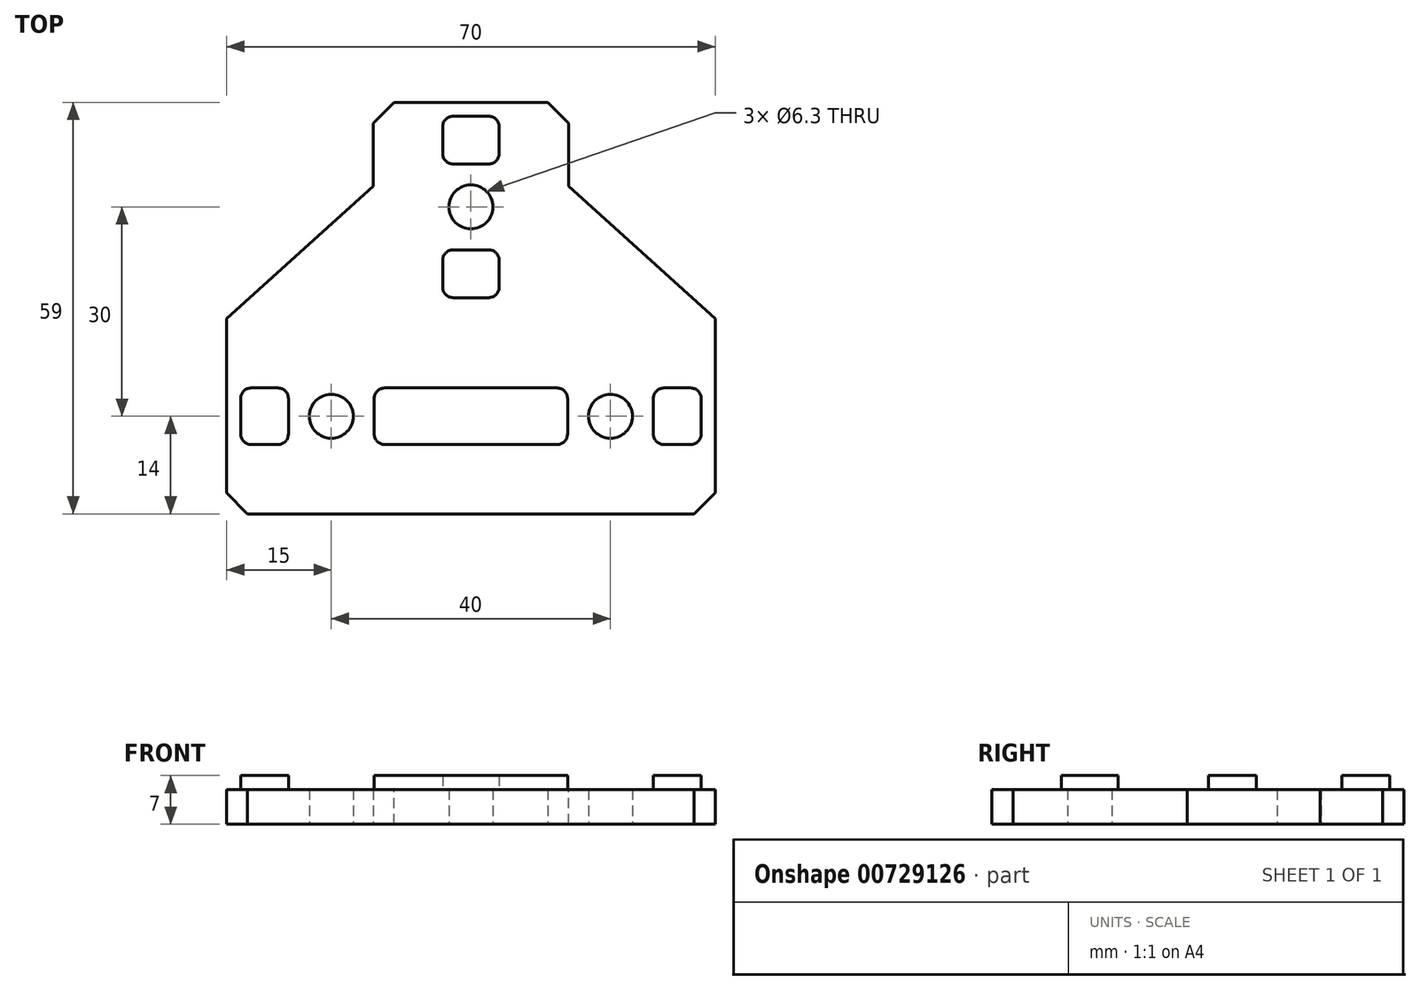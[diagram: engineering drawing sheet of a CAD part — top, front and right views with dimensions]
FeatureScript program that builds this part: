
annotation { "Feature Type Name" : "Feature", "Feature Type Description" : "" }
export const myFeature = defineFeature(function(context is Context, id is Id, definition is map)
    precondition{}
    {
        {
            var Q0;
            Q0=qCreatedBy(makeId("Top.planeOp"),FACE);
            var sketch = newSketch(context, id + "F0", { "sketchPlane" : qUnion([Q0])});
            skLineSegment(sketch, "E0", {"start": v(-35, 0) * mm, "end": v(-35, 28) * mm});
            skLineSegment(sketch, "E1", {"start": v(-35, 28) * mm, "end": v(-14, 47) * mm});
            skLineSegment(sketch, "E2", {"start": v(14, 47) * mm, "end": v(35, 28) * mm});
            skLineSegment(sketch, "E3", {"start": v(35, 28) * mm, "end": v(35, 0) * mm});
            skLineSegment(sketch, "E4", {"start": v(35, 0) * mm, "end": v(-35, 0) * mm});
            skPoint(sketch, "E5", {"position": v(0, 0) * mm});
            skLineSegment(sketch, "E6", {"start": v(-14, 47) * mm, "end": v(-14, 59) * mm});
            skLineSegment(sketch, "E7", {"start": v(-14, 59) * mm, "end": v(14, 59) * mm});
            skLineSegment(sketch, "E8", {"start": v(14, 59) * mm, "end": v(14, 47) * mm});
            skPoint(sketch, "E9", {"position": v(0, 59) * mm});
            skPoint(sketch, "E10.centerSnap0", {"position": v(-35, 14) * mm});
            skPoint(sketch, "E11.centerSnap0", {"position": v(35, 14) * mm});
            skPoint(sketch, "E12", {"position": v(0, 44) * mm});
            skPoint(sketch, "E13", {"position": v(-20, 14) * mm});
            skPoint(sketch, "E14", {"position": v(20, 14) * mm});
            skSolve(sketch);
        }
        {
            var Q0;
            Q0=makeQuery(id+"F0.imprint","IMPRINT",FACE,{"disambiguationData":[TD([[makeQuery(id+"F0.imprint","IMPRINT",EDGE,{"derivedFrom":sQuery(id+"F0.wireOp",EDGE,"E0")}),-1.0]])]});
            extrude(context, id + "F1", {"entities" : qUnion([Q0]), "oppositeDirection" : true, "depth" : 5 * mm, "offsetDistance" : 25 * mm});
        }
        {
            var Q0;
            Q0=sQuery(id+"F0.wireOp",VERTEX,"E14");
            var Q1;
            Q1=sQuery(id+"F0.wireOp",VERTEX,"E13");
            var Q2;
            Q2=sQuery(id+"F0.wireOp",VERTEX,"E12");
            var Q3;
            Q3=makeQuery(id+"F1.opExtrude","SWEPT_BODY",BODY,{"disambiguationData":[OSD([sQuery(id+"F0.wireOp",EDGE,"E0"),sQuery(id+"F0.wireOp",EDGE,"E1"),sQuery(id+"F0.wireOp",EDGE,"E2"),sQuery(id+"F0.wireOp",EDGE,"E3"),sQuery(id+"F0.wireOp",EDGE,"E4"),sQuery(id+"F0.wireOp",EDGE,"E6"),sQuery(id+"F0.wireOp",EDGE,"E7"),sQuery(id+"F0.wireOp",EDGE,"E8")])]});
            hole(context, id + "F2", {"style" : HoleStyle.SIMPLE, "endStyle" : HoleEndStyle.THROUGH, "holeDiameter" : 6.3 * mm, "majorDiameter" : 5 * mm, "isTappedThrough" : true, "tappedDepth" : 12 * mm, "tapClearance" : 3, "locations" : qUnion([Q0, Q1, Q2]), "scope" : qUnion([Q3]), "startStyle" : HoleStartStyle.PART});
        }
        {
            var Q0;
            Q0=makeQuery(id+"F1.opExtrude","SWEPT_EDGE",EDGE,{"disambiguationData":[OSD([sQuery(id+"F0.wireOp",EDGE,"E7"),sQuery(id+"F0.wireOp",EDGE,"E8")])]});
            var Q1;
            Q1=makeQuery(id+"F1.opExtrude","SWEPT_EDGE",EDGE,{"disambiguationData":[OSD([sQuery(id+"F0.wireOp",EDGE,"E6"),sQuery(id+"F0.wireOp",EDGE,"E7")])]});
            var Q2;
            Q2=makeQuery(id+"F1.opExtrude","SWEPT_EDGE",EDGE,{"disambiguationData":[OSD([sQuery(id+"F0.wireOp",EDGE,"E3"),sQuery(id+"F0.wireOp",EDGE,"E4")])]});
            var Q3;
            Q3=makeQuery(id+"F1.opExtrude","SWEPT_EDGE",EDGE,{"disambiguationData":[OSD([sQuery(id+"F0.wireOp",EDGE,"E0"),sQuery(id+"F0.wireOp",EDGE,"E4")])]});
            chamfer(context, id + "F3", {"entities" : qUnion([Q0, Q1, Q2, Q3]), "width" : 3 * mm, "tangentPropagation" : true});
        }
        {
            var Q0;
            Q0=makeQuery(id+"F1.opExtrude","CAP_FACE",FACE,{"disambiguationData":[OSD([sQuery(id+"F0.wireOp",EDGE,"E0"),sQuery(id+"F0.wireOp",EDGE,"E1"),sQuery(id+"F0.wireOp",EDGE,"E2"),sQuery(id+"F0.wireOp",EDGE,"E3"),sQuery(id+"F0.wireOp",EDGE,"E4"),sQuery(id+"F0.wireOp",EDGE,"E6"),sQuery(id+"F0.wireOp",EDGE,"E7"),sQuery(id+"F0.wireOp",EDGE,"E8")])],"isStart":true});
            var sketch = newSketch(context, id + "F4", { "sketchPlane" : qUnion([Q0])});
            skLineSegment(sketch, "E15.bottom", {"start": v(-26.15, 18.05) * mm, "end": v(-33, 18.05) * mm});
            skLineSegment(sketch, "E15.top", {"start": v(-26.15, 9.95) * mm, "end": v(-33, 9.95) * mm});
            skLineSegment(sketch, "E15.left", {"start": v(-26.15, 18.05) * mm, "end": v(-26.15, 9.95) * mm});
            skLineSegment(sketch, "E15.right", {"start": v(-33, 18.05) * mm, "end": v(-33, 9.95) * mm});
            skLineSegment(sketch, "E16.bottom", {"start": v(-13.85, 18.05) * mm, "end": v(13.85, 18.05) * mm});
            skLineSegment(sketch, "E16.top", {"start": v(-13.85, 9.95) * mm, "end": v(13.85, 9.95) * mm});
            skLineSegment(sketch, "E16.left", {"start": v(-13.85, 18.05) * mm, "end": v(-13.85, 9.95) * mm});
            skLineSegment(sketch, "E16.right", {"start": v(13.85, 18.05) * mm, "end": v(13.85, 9.95) * mm});
            skLineSegment(sketch, "E17.bottom", {"start": v(33, 9.95) * mm, "end": v(26.15, 9.95) * mm});
            skLineSegment(sketch, "E17.top", {"start": v(33, 18.05) * mm, "end": v(26.15, 18.05) * mm});
            skLineSegment(sketch, "E17.left", {"start": v(33, 9.95) * mm, "end": v(33, 18.05) * mm});
            skLineSegment(sketch, "E17.right", {"start": v(26.15, 9.95) * mm, "end": v(26.15, 18.05) * mm});
            skLineSegment(sketch, "E18.bottom", {"start": v(-4.05, 37.85) * mm, "end": v(4.05, 37.85) * mm});
            skLineSegment(sketch, "E18.top", {"start": v(-4.05, 31) * mm, "end": v(4.05, 31) * mm});
            skLineSegment(sketch, "E18.left", {"start": v(-4.05, 37.85) * mm, "end": v(-4.05, 31) * mm});
            skLineSegment(sketch, "E18.right", {"start": v(4.05, 37.85) * mm, "end": v(4.05, 31) * mm});
            skLineSegment(sketch, "E19.bottom", {"start": v(-4.05, 57) * mm, "end": v(4.05, 57) * mm});
            skLineSegment(sketch, "E19.top", {"start": v(-4.05, 50.15) * mm, "end": v(4.05, 50.15) * mm});
            skLineSegment(sketch, "E19.left", {"start": v(-4.05, 57) * mm, "end": v(-4.05, 50.15) * mm});
            skLineSegment(sketch, "E19.right", {"start": v(4.05, 57) * mm, "end": v(4.05, 50.15) * mm});
            skPoint(sketch, "E20", {"position": v(-26.15, 14) * mm});
            skPoint(sketch, "E21", {"position": v(13.85, 14) * mm});
            skPoint(sketch, "E22", {"position": v(33, 14) * mm});
            skPoint(sketch, "E23", {"position": v(-20, 14) * mm});
            skPoint(sketch, "E24", {"position": v(0, 44) * mm});
            skPoint(sketch, "E25", {"position": v(0, 37.85) * mm});
            skPoint(sketch, "E26", {"position": v(0, 57) * mm});
            skSolve(sketch);
        }
        {
            var Q0;
            Q0=makeQuery(id+"F4.imprint","IMPRINT",FACE,{"disambiguationData":[TD([[makeQuery(id+"F4.imprint","IMPRINT",EDGE,{"derivedFrom":sQuery(id+"F4.wireOp",EDGE,"E19.bottom")}),-1.0]])]});
            var Q1;
            Q1=makeQuery(id+"F4.imprint","IMPRINT",FACE,{"disambiguationData":[TD([[makeQuery(id+"F4.imprint","IMPRINT",EDGE,{"derivedFrom":sQuery(id+"F4.wireOp",EDGE,"E18.bottom")}),-1.0]])]});
            var Q2;
            Q2=makeQuery(id+"F4.imprint","IMPRINT",FACE,{"disambiguationData":[TD([[makeQuery(id+"F4.imprint","IMPRINT",EDGE,{"derivedFrom":sQuery(id+"F4.wireOp",EDGE,"E17.bottom")}),-1.0]])]});
            var Q3;
            Q3=makeQuery(id+"F4.imprint","IMPRINT",FACE,{"disambiguationData":[TD([[makeQuery(id+"F4.imprint","IMPRINT",EDGE,{"derivedFrom":sQuery(id+"F4.wireOp",EDGE,"E16.bottom")}),-1.0]])]});
            var Q4;
            Q4=makeQuery(id+"F4.imprint","IMPRINT",FACE,{"disambiguationData":[TD([[makeQuery(id+"F4.imprint","IMPRINT",EDGE,{"derivedFrom":sQuery(id+"F4.wireOp",EDGE,"E15.bottom")}),1.0]])]});
            extrude(context, id + "F5", {"entities" : qUnion([Q0, Q1, Q2, Q3, Q4]), "operationType" : NewBodyOperationType.ADD, "depth" : 2 * mm, "offsetDistance" : 25 * mm});
        }
        {
            var Q0;
            Q0=makeQuery(id+"F5.opExtrude","SWEPT_EDGE",EDGE,{"disambiguationData":[OSD([sQuery(id+"F4.wireOp",EDGE,"E15.top"),sQuery(id+"F4.wireOp",EDGE,"E15.left")])]});
            var Q1;
            Q1=makeQuery(id+"F5.opExtrude","SWEPT_EDGE",EDGE,{"disambiguationData":[OSD([sQuery(id+"F4.wireOp",EDGE,"E15.top"),sQuery(id+"F4.wireOp",EDGE,"E15.right")])]});
            var Q2;
            Q2=makeQuery(id+"F5.opExtrude","SWEPT_EDGE",EDGE,{"disambiguationData":[OSD([sQuery(id+"F4.wireOp",EDGE,"E15.bottom"),sQuery(id+"F4.wireOp",EDGE,"E15.right")])]});
            var Q3;
            Q3=makeQuery(id+"F5.opExtrude","SWEPT_EDGE",EDGE,{"disambiguationData":[OSD([sQuery(id+"F4.wireOp",EDGE,"E15.bottom"),sQuery(id+"F4.wireOp",EDGE,"E15.left")])]});
            var Q4;
            Q4=makeQuery(id+"F5.opExtrude","SWEPT_EDGE",EDGE,{"disambiguationData":[OSD([sQuery(id+"F4.wireOp",EDGE,"E16.top"),sQuery(id+"F4.wireOp",EDGE,"E16.left")])]});
            var Q5;
            Q5=makeQuery(id+"F5.opExtrude","SWEPT_EDGE",EDGE,{"disambiguationData":[OSD([sQuery(id+"F4.wireOp",EDGE,"E16.bottom"),sQuery(id+"F4.wireOp",EDGE,"E16.left")])]});
            var Q6;
            Q6=makeQuery(id+"F5.opExtrude","SWEPT_EDGE",EDGE,{"disambiguationData":[OSD([sQuery(id+"F4.wireOp",EDGE,"E16.top"),sQuery(id+"F4.wireOp",EDGE,"E16.right")])]});
            var Q7;
            Q7=makeQuery(id+"F5.opExtrude","SWEPT_EDGE",EDGE,{"disambiguationData":[OSD([sQuery(id+"F4.wireOp",EDGE,"E16.bottom"),sQuery(id+"F4.wireOp",EDGE,"E16.right")])]});
            var Q8;
            Q8=makeQuery(id+"F5.opExtrude","SWEPT_EDGE",EDGE,{"disambiguationData":[OSD([sQuery(id+"F4.wireOp",EDGE,"E17.top"),sQuery(id+"F4.wireOp",EDGE,"E17.left")])]});
            var Q9;
            Q9=makeQuery(id+"F5.opExtrude","SWEPT_EDGE",EDGE,{"disambiguationData":[OSD([sQuery(id+"F4.wireOp",EDGE,"E17.bottom"),sQuery(id+"F4.wireOp",EDGE,"E17.left")])]});
            var Q10;
            Q10=makeQuery(id+"F5.opExtrude","SWEPT_EDGE",EDGE,{"disambiguationData":[OSD([sQuery(id+"F4.wireOp",EDGE,"E17.bottom"),sQuery(id+"F4.wireOp",EDGE,"E17.right")])]});
            var Q11;
            Q11=makeQuery(id+"F5.opExtrude","SWEPT_EDGE",EDGE,{"disambiguationData":[OSD([sQuery(id+"F4.wireOp",EDGE,"E17.top"),sQuery(id+"F4.wireOp",EDGE,"E17.right")])]});
            var Q12;
            Q12=makeQuery(id+"F5.opExtrude","SWEPT_EDGE",EDGE,{"disambiguationData":[OSD([sQuery(id+"F4.wireOp",EDGE,"E18.top"),sQuery(id+"F4.wireOp",EDGE,"E18.right")])]});
            var Q13;
            Q13=makeQuery(id+"F5.opExtrude","SWEPT_EDGE",EDGE,{"disambiguationData":[OSD([sQuery(id+"F4.wireOp",EDGE,"E18.top"),sQuery(id+"F4.wireOp",EDGE,"E18.left")])]});
            var Q14;
            Q14=makeQuery(id+"F5.opExtrude","SWEPT_EDGE",EDGE,{"disambiguationData":[OSD([sQuery(id+"F4.wireOp",EDGE,"E18.bottom"),sQuery(id+"F4.wireOp",EDGE,"E18.right")])]});
            var Q15;
            Q15=makeQuery(id+"F5.opExtrude","SWEPT_EDGE",EDGE,{"disambiguationData":[OSD([sQuery(id+"F4.wireOp",EDGE,"E18.bottom"),sQuery(id+"F4.wireOp",EDGE,"E18.left")])]});
            var Q16;
            Q16=makeQuery(id+"F5.opExtrude","SWEPT_EDGE",EDGE,{"disambiguationData":[OSD([sQuery(id+"F4.wireOp",EDGE,"E19.bottom"),sQuery(id+"F4.wireOp",EDGE,"E19.right")])]});
            var Q17;
            Q17=makeQuery(id+"F5.opExtrude","SWEPT_EDGE",EDGE,{"disambiguationData":[OSD([sQuery(id+"F4.wireOp",EDGE,"E19.top"),sQuery(id+"F4.wireOp",EDGE,"E19.right")])]});
            var Q18;
            Q18=makeQuery(id+"F5.opExtrude","SWEPT_EDGE",EDGE,{"disambiguationData":[OSD([sQuery(id+"F4.wireOp",EDGE,"E19.bottom"),sQuery(id+"F4.wireOp",EDGE,"E19.left")])]});
            var Q19;
            Q19=makeQuery(id+"F5.opExtrude","SWEPT_EDGE",EDGE,{"disambiguationData":[OSD([sQuery(id+"F4.wireOp",EDGE,"E19.top"),sQuery(id+"F4.wireOp",EDGE,"E19.left")])]});
            fillet(context, id + "F6", {"entities" : qUnion([Q0, Q1, Q2, Q3, Q4, Q5, Q6, Q7, Q8, Q9, Q10, Q11, Q12, Q13, Q14, Q15, Q16, Q17, Q18, Q19]), "radius" : 1.5 * mm, "tangentPropagation" : true, "allowEdgeOverflow" : false});
        }
    });
